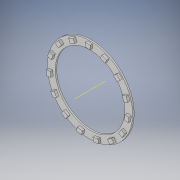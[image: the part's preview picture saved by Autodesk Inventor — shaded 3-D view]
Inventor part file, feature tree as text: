
AUTODESK INVENTOR PART (.ipt)
format: ipt  version: 2019.2 (Build 232265000, 265)  size: 167,936 bytes
history: native  units: in
note: dims shown in document units (in); Inventor stores cm internally (conversion verified against a paired STEP export)
features: other x14, extrude x2, sketch x2, pattern_circular x1
ambient origin geometry x8: Origin, YZ Plane, XZ Plane, XY Plane, X Axis, Y Axis, Z Axis, Center Point
bodies: Solid1 (feature_tree)
feature tree (19):
  extrude  "Extrusion1"  Depth=2.3622in
  extrude  "Extrusion2"  Depth=0.0669in TaperAngle=0.0deg
  pattern_circular  "Circular Pattern1"  Count=15 Angle=360.0deg
  sketch  "Sketch1"  dims[d0=1.9291in d1=2.3622in]
  sketch  "Sketch2"  dims[d2=0.0433in d3=0.0in d4=0.0669in d5=0.0in d6=5.9055in d7=360.0deg]
  other  "Work Axis1"
  other  "Work Axis2"
  other  "Work Axis3"
  other  "Work Axis4"
  other  "Work Axis5"
  other  "Work Axis6"
  other  "Work Axis7"
  other  "Work Axis8"
  other  "Work Axis9"
  other  "Work Axis10"
  other  "Work Axis11"
  other  "Work Axis12"
  other  "Work Axis13"
  other  "Work Axis14"
